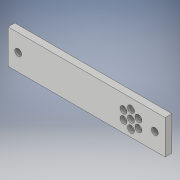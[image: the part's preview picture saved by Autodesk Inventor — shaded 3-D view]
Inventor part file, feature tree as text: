
AUTODESK INVENTOR PART (.ipt)
format: ipt  version: 2019 (Build 230136000, 136)  size: 139,776 bytes
history: native  units: in
note: dims shown in document units (in); Inventor stores cm internally (conversion verified against a paired STEP export)
features: sketch x3, hole x3, extrude x1, projected_geometry x1
ambient origin geometry x8: Origin, YZ Plane, XZ Plane, XY Plane, X Axis, Y Axis, Z Axis, Center Point
bodies: Solid1 (feature_tree)
feature tree (8):
  extrude  "Extrusion1"  Depth=1.25in
  sketch  "Sketch2"  dims[d2=0.25in d3=0.0in d6=0.575in]
  hole  "Hole2"  [1 undecoded]
  hole  "Hole3"  [1 undecoded]
  hole  "Hole4"  [1 undecoded]
  sketch  "Sketch1"  dims[d0=5.75in d1=1.25in]
  sketch  "Sketch5"  dims[d7=90.0deg d9=0.63in d17=1.25in d46=2.3622in d48=360.0deg d50=0.134in d51=0.25in d52=0.256in d53=0.134in d54=0.5635in d55=0.3in d56=0.8108in d57=0.25in d58=0.25in d59=0.256in d60=0.134in d61=0.5635in d62=0.3in d63=0.8108in d64=1.25in d65=0.625in d68=0.625in d69=0.375in d71=0.375in d72=0.25in d73=0.25in d74=0.256in d75=0.134in d76=0.5635in d77=0.3in d78=0.8108in]
  projected_geometry  "Projected Loop1"
note: 3 required parameter values undecoded (feature->parameter linkage not recoverable at this tier; creation-order binding heuristic only, values carry confidence <= 0.55)
